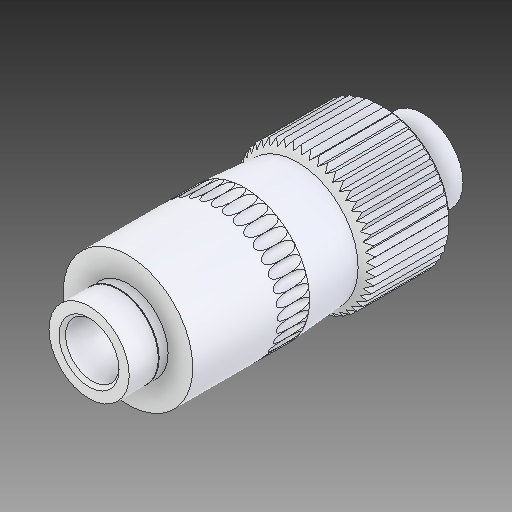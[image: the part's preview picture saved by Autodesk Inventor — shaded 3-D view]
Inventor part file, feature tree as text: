
AUTODESK INVENTOR PART (.ipt)
format: ipt  version: 2018 (Build 220112000, 112)  size: 699,904 bytes
history: native  units: in
note: dims shown in document units (in); Inventor stores cm internally (conversion verified against a paired STEP export)
features: sketch x3, revolve x2, pattern_circular x2, plane x2, extrude x1, chamfer x1
ambient origin geometry x8: Origin, YZ Plane, XZ Plane, XY Plane, X Axis, Y Axis, Z Axis, Center Point
bodies: Solid1 (feature_tree)
feature tree (11):
  revolve  "Revolution1"  [1 undecoded]
  extrude  "Extrusion1"  Depth=0.002in
  pattern_circular  "Circular Pattern1"  [2 undecoded]
  plane  "Work Plane1"
  revolve  "Revolution2"  Angle=135.0deg
  pattern_circular  "Circular Pattern2"  [2 undecoded]
  chamfer  "Chamfer1"  Distance=0.315in
  plane  "Work Plane2"
  sketch  "Sketch1"  dims[d0=0.1299in d1=0.1949in]
  sketch  "Sketch2"  dims[d3=0.002in d4=0.002in]
  sketch  "Sketch3"  dims[d5=0.0709in d6=0.3386in d7=135.0deg d8=0.0945in d9=0.315in d10=0.1772in d11=135.0deg d12=0.2953in d13=0.002in d14=0.002in d16=0.811in d17=0.0709in d19=0.315in d20=0.0945in d21=90.0deg d22=0.2835in d23=0.3386in d24=0.0247in d26=0.1575in d27=0.2362in d28=0.0in d29=19.685in d30=360.0deg d32=-0.2441in d33=0.2264in d35=0.1614in d36=0.315in d37=0.0275in d38=90.0deg d40=14.1732in d41=360.0deg d46=0.0079in d47=0.0787in d48=45.0deg d49=0.1949in d50=-0.1949in]
note: 5 required parameter values undecoded (feature->parameter linkage not recoverable at this tier; creation-order binding heuristic only, values carry confidence <= 0.55)